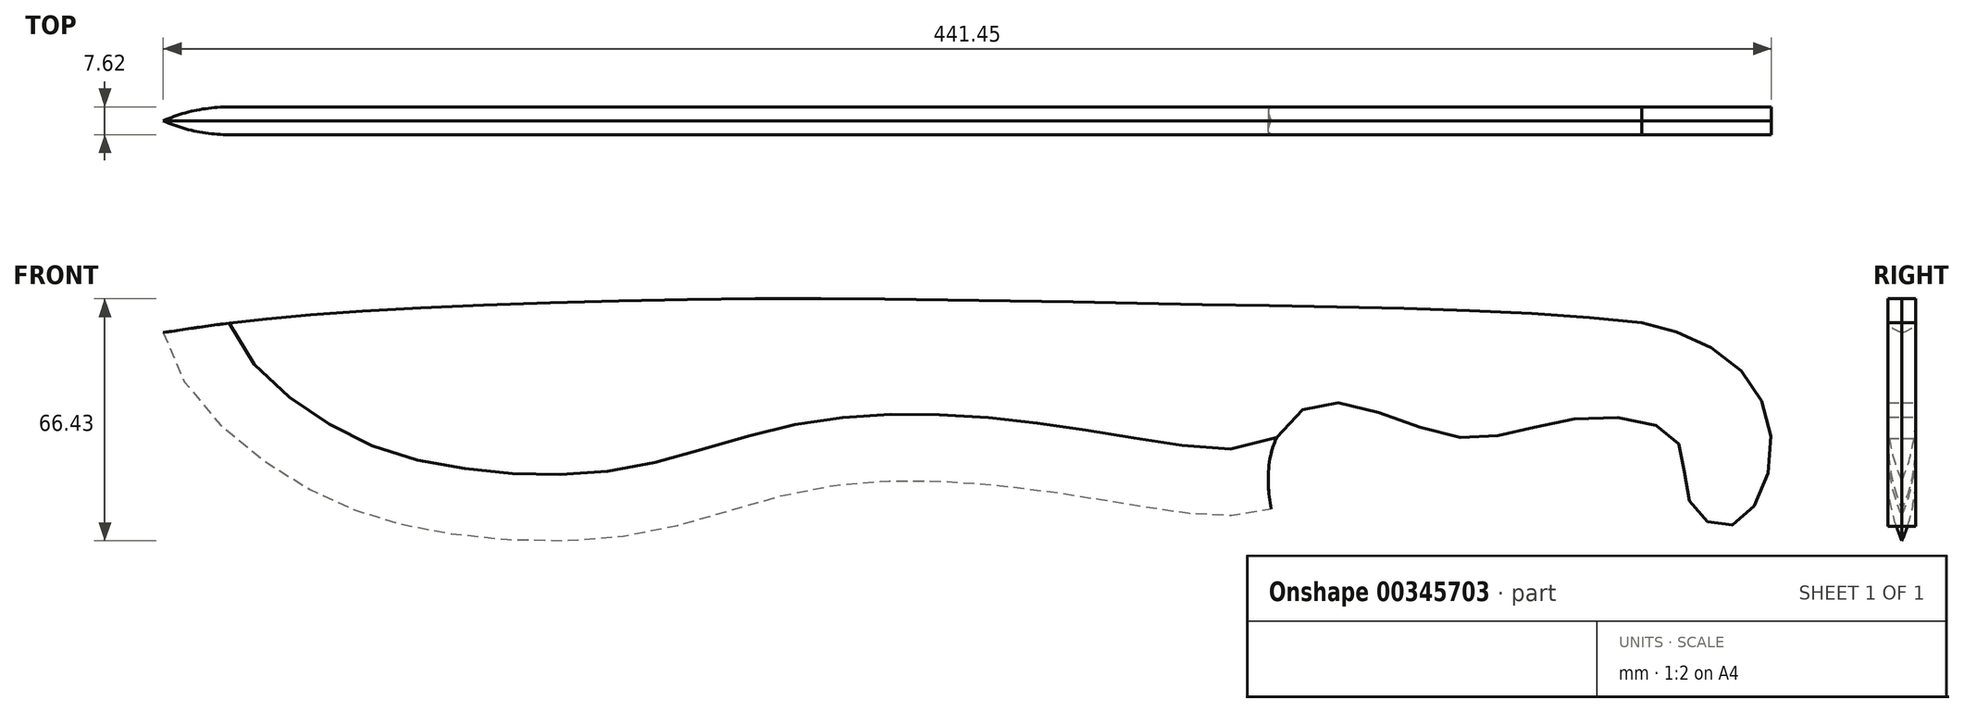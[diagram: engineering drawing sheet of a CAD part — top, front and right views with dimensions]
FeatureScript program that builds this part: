
annotation { "Feature Type Name" : "Feature", "Feature Type Description" : "" }
export const myFeature = defineFeature(function(context is Context, id is Id, definition is map)
    precondition{}
    {
        {
            var Q0;
            Q0=qCreatedBy(makeId("Front.planeOp"),FACE);
            var sketch = newSketch(context, id + "F0", { "sketchPlane" : qUnion([Q0])});
            skFitSpline(sketch, "E0", {"points": [v(136.5, 63.88) * mm, v(15.37, 68.82) * mm, v(-110.05, 70.36) * mm, v(-231.63, 65.74) * mm, v(-269.33, 61.12) * mm], "startDerivative": vector(-337.04, 40.16) * mm, "endDerivative": vector(-195.96, -30.03) * mm});
            skFitSpline(sketch, "E1", {"points": [v(-269.33, 61.12) * mm, v(-235.58, 21.88) * mm, v(-195.67, 6.82) * mm, v(-138.9, 5.93) * mm, v(-89.6, 18.52) * mm, v(-36.35, 18.83) * mm, v(3.7, 12.76) * mm, v(34.78, 12.75) * mm], "startDerivative": vector(73.29, -329) * mm, "endDerivative": vector(238.15, 76.76) * mm});
            skFitSpline(sketch, "E2", {"points": [v(136.5, 63.88) * mm, v(162.92, 51.55) * mm, v(171.92, 26.5) * mm, v(160.84, 8.17) * mm, v(149.6, 15.04) * mm, v(145.8, 31.93) * mm, v(116.74, 37.25) * mm, v(85.91, 32.4) * mm, v(49.8, 41.8) * mm, v(34.78, 12.75) * mm], "startDerivative": vector(217.45, -45.44) * mm, "endDerivative": vector(81.04, -445.48) * mm});
            skSolve(sketch);
        }
        {
            var Q0;
            Q0=makeQuery(id+"F0.imprint","IMPRINT",FACE,{"disambiguationData":[TD([[makeQuery(id+"F0.imprint","IMPRINT",EDGE,{"derivedFrom":sQuery(id+"F0.wireOp",EDGE,"E0")}),1.0]])]});
            extrude(context, id + "F1", {"entities" : qUnion([Q0]), "depth" : 3.8 * mm});
        }
        {
            var Q0;
            Q0=makeQuery(id+"F1.opExtrude","CAP_EDGE",EDGE,{"disambiguationData":[OSD([sQuery(id+"F0.wireOp",EDGE,"E1")])],"isStart":false});
            fillet(context, id + "F2", {"entities" : qUnion([Q0]), "radius" : 45.38 * mm, "tangentPropagation" : true, "allowEdgeOverflow" : false});
        }
        {
            var Q0;
            Q0=makeQuery(id+"F1.opExtrude","SWEPT_BODY",BODY,{"disambiguationData":[OSD([sQuery(id+"F0.wireOp",EDGE,"E0"),sQuery(id+"F0.wireOp",EDGE,"E1"),sQuery(id+"F0.wireOp",EDGE,"E2")])]});
            transform(context, id + "F3", {"entities" : qUnion([Q0]), "transformType" : TransformType.COPY});
        }
        {
            var Q0;
            Q0=makeQuery(id+"F3.opPattern","COPY",BODY,{"derivedFrom":makeQuery(id+"F1.opExtrude","SWEPT_BODY",BODY,{"disambiguationData":[OSD([sQuery(id+"F0.wireOp",EDGE,"E0"),sQuery(id+"F0.wireOp",EDGE,"E1"),sQuery(id+"F0.wireOp",EDGE,"E2")])]}),"instanceName":"1"});
            var Q1;
            Q1=qCreatedBy(makeId("Front.planeOp"),FACE);
            mirror(context, id + "F4", {"entities" : qUnion([Q0]), "mirrorPlane" : qUnion([Q1])});
        }
    });
